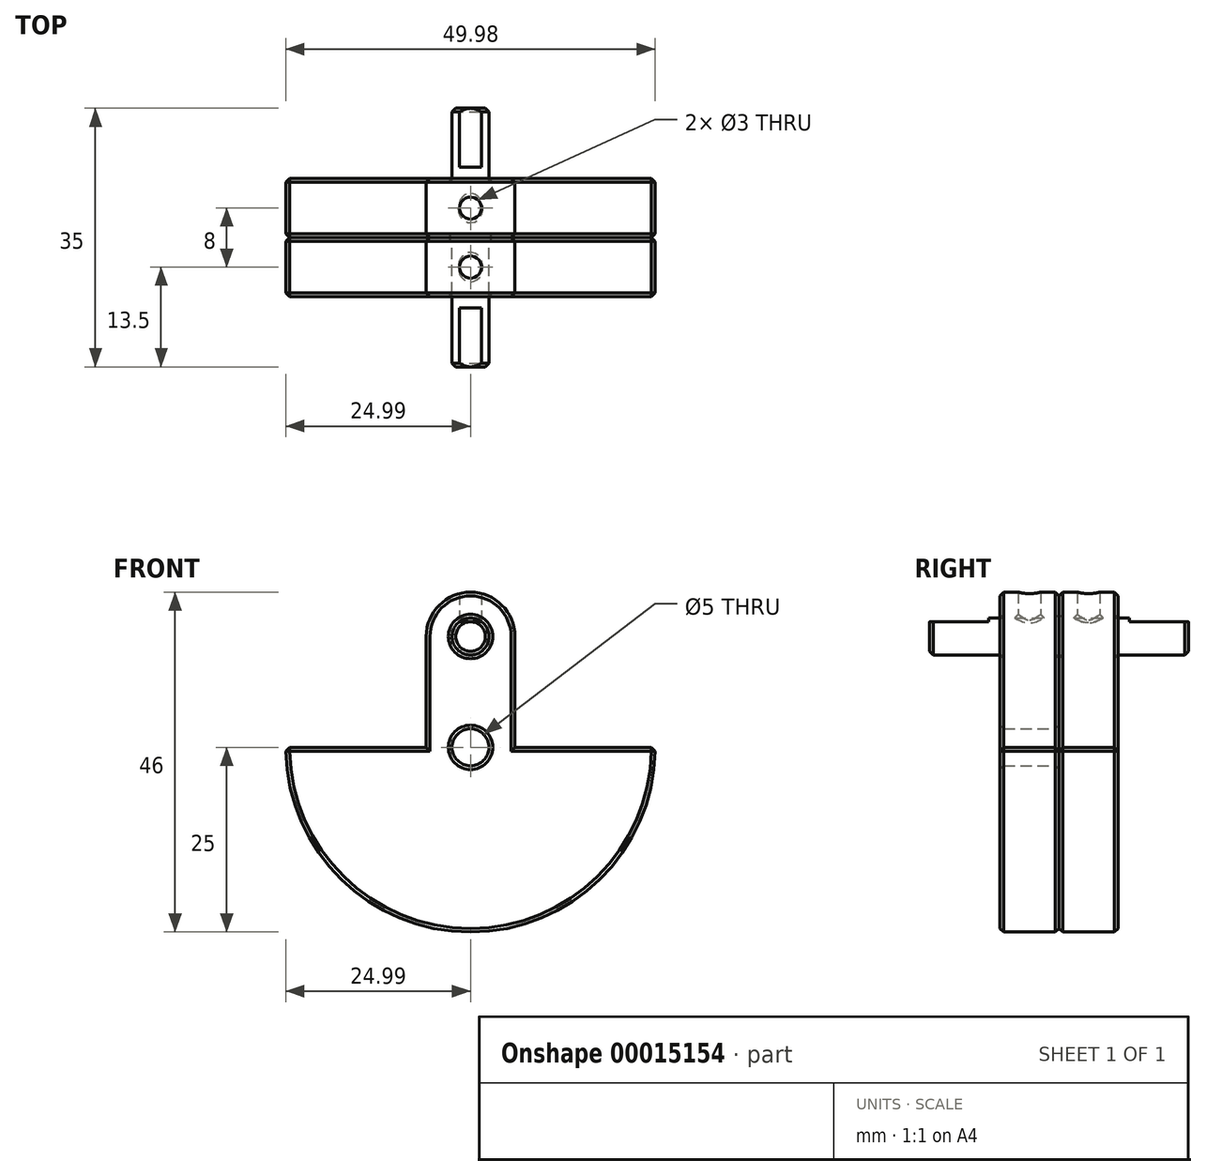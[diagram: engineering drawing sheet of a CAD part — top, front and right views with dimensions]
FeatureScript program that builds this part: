
annotation { "Feature Type Name" : "Feature", "Feature Type Description" : "" }
export const myFeature = defineFeature(function(context is Context, id is Id, definition is map)
    precondition{}
    {
        {
            var Q0;
            Q0=qCreatedBy(makeId("Front.planeOp"),FACE);
            var sketch = newSketch(context, id + "F0", { "sketchPlane" : qUnion([Q0])});
            skCircle(sketch, "E0", {"center": v(0, 0) * mm, "radius": 2.5 * mm});
            skCircle(sketch, "E1", {"center": v(0, 15) * mm, "radius": 2.5 * mm});
            skArc(sketch, "E2", {"start": v(6, 15) * mm, "mid": v(0, 21) * mm, "end": v(-6, 15) * mm});
            skLineSegment(sketch, "E3", {"start": v(-25, 0) * mm, "end": v(-6, 0) * mm});
            skLineSegment(sketch, "E4", {"start": v(-6, 15) * mm, "end": v(-6, 0) * mm});
            skLineSegment(sketch, "E5", {"start": v(6, 15) * mm, "end": v(6, 0) * mm});
            skArc(sketch, "E6", {"start": v(-25, 0) * mm, "mid": v(0, -25) * mm, "end": v(25, 0) * mm});
            skArc(sketch, "E7", {"start": v(25, 0) * mm, "mid": v(0, 25) * mm, "end": v(-25, 0) * mm, "construction": true});
            skLineSegment(sketch, "E8.trimOffspring", {"start": v(6, 0) * mm, "end": v(25, 0) * mm});
            skSolve(sketch);
        }
        {
            var Q0;
            Q0=makeQuery(id+"F0.imprint","IMPRINT",FACE,{"disambiguationData":[TD([[makeQuery(id+"F0.imprint","IMPRINT",EDGE,{"derivedFrom":sQuery(id+"F0.wireOp",EDGE,"E0")}),-1.0]])]});
            extrude(context, id + "F1", {"entities" : qUnion([Q0]), "depth" : 8 * mm});
        }
        {
            var Q0;
            Q0=makeQuery(id+"F0.imprint","IMPRINT",FACE,{"disambiguationData":[TD([[makeQuery(id+"F0.imprint","IMPRINT",EDGE,{"derivedFrom":sQuery(id+"F0.wireOp",EDGE,"E0")}),-1.0]])]});
            var Q1;
            Q1=makeQuery(id+"F0.imprint","IMPRINT",FACE,{"disambiguationData":[TD([[makeQuery(id+"F0.imprint","IMPRINT",EDGE,{"derivedFrom":sQuery(id+"F0.wireOp",EDGE,"E0")}),1.0]])]});
            extrude(context, id + "F2", {"entities" : qUnion([Q0, Q1]), "oppositeDirection" : true, "depth" : 8 * mm});
        }
        {
            var Q0;
            Q0=qCreatedBy(makeId("Top.planeOp"),FACE);
            cPlane(context, id + "F3", {"entities" : qUnion([Q0]), "cplaneType" : CPlaneType.OFFSET, "offset" : 15 * mm, "width" : 150 * mm, "height" : 150 * mm});
        }
        {
            var Q0;
            Q0=qCreatedBy(id+"F3.planeOp",FACE);
            var sketch = newSketch(context, id + "F4", { "sketchPlane" : qUnion([Q0])});
            skLineSegment(sketch, "E9", {"start": v(0, 14.38) * mm, "end": v(0, -14.54) * mm, "construction": true});
            skCircle(sketch, "E10", {"center": v(0, 4) * mm, "radius": 1.5 * mm});
            skCircle(sketch, "E11", {"center": v(0, -4) * mm, "radius": 1.5 * mm});
            skSolve(sketch);
        }
        {
            var Q0;
            Q0=makeQuery(id+"F4.imprint","IMPRINT",FACE,{"disambiguationData":[TD([[makeQuery(id+"F4.imprint","IMPRINT",EDGE,{"derivedFrom":sQuery(id+"F4.wireOp",EDGE,"E10")}),1.0]])]});
            var Q1;
            Q1=makeQuery(id+"F4.imprint","IMPRINT",FACE,{"disambiguationData":[TD([[makeQuery(id+"F4.imprint","IMPRINT",EDGE,{"derivedFrom":sQuery(id+"F4.wireOp",EDGE,"E11")}),1.0]])]});
            var Q2;
            Q2=sQuery(id+"F4.wireOp",EDGE,"E11");
            var Q3;
            Q3=sQuery(id+"F4.wireOp",EDGE,"E10");
            extrude(context, id + "F5", {"entities" : qUnion([Q0, Q1]), "operationType" : NewBodyOperationType.REMOVE, "surfaceEntities" : qUnion([Q2, Q3]), "endBound" : BoundingType.THROUGH_ALL, "depth" : 25 * mm});
        }
        {
            var Q0;
            Q0=makeQuery(id+"F1.opExtrude","CAP_EDGE",EDGE,{"disambiguationData":[OSD([sQuery(id+"F0.wireOp",EDGE,"E6")])],"isStart":false});
            var Q1;
            Q1=makeQuery(id+"F1.opExtrude","SWEPT_FACE",FACE,{"disambiguationData":[OSD([sQuery(id+"F0.wireOp",EDGE,"E0")])]});
            var Q2;
            Q2=makeQuery(id+"F1.opExtrude","SWEPT_FACE",FACE,{"disambiguationData":[OSD([sQuery(id+"F0.wireOp",EDGE,"E1")])]});
            var Q3;
            Q3=makeQuery(id+"F2.opExtrude","SWEPT_FACE",FACE,{"disambiguationData":[OSD([sQuery(id+"F0.wireOp",EDGE,"E1")])]});
            var Q4;
            Q4=makeQuery(id+"F2.opExtrude","CAP_EDGE",EDGE,{"disambiguationData":[OSD([sQuery(id+"F0.wireOp",EDGE,"E6")])],"isStart":false});
            var Q5;
            Q5=makeQuery(id+"F2.opExtrude","CAP_EDGE",EDGE,{"disambiguationData":[OSD([sQuery(id+"F0.wireOp",EDGE,"E4")])],"isStart":false});
            var Q6;
            Q6=makeQuery(id+"F2.opExtrude","CAP_EDGE",EDGE,{"disambiguationData":[OSD([sQuery(id+"F0.wireOp",EDGE,"E5")])],"isStart":false});
            var Q7;
            Q7=makeQuery(id+"F1.opExtrude","CAP_EDGE",EDGE,{"disambiguationData":[OSD([sQuery(id+"F0.wireOp",EDGE,"E5")])],"isStart":false});
            var Q8;
            Q8=makeQuery(id+"F1.opExtrude","CAP_FACE",FACE,{"disambiguationData":[OSD([sQuery(id+"F0.wireOp",EDGE,"E0"),sQuery(id+"F0.wireOp",EDGE,"E1"),sQuery(id+"F0.wireOp",EDGE,"E2"),sQuery(id+"F0.wireOp",EDGE,"E3"),sQuery(id+"F0.wireOp",EDGE,"E4"),sQuery(id+"F0.wireOp",EDGE,"E5"),sQuery(id+"F0.wireOp",EDGE,"E6"),sQuery(id+"F0.wireOp",EDGE,"E8.trimOffspring")])],"isStart":false});
            var Q9;
            Q9=makeQuery(id+"F2.opExtrude","CAP_FACE",FACE,{"disambiguationData":[OSD([sQuery(id+"F0.wireOp",EDGE,"E1"),sQuery(id+"F0.wireOp",EDGE,"E2"),sQuery(id+"F0.wireOp",EDGE,"E3"),sQuery(id+"F0.wireOp",EDGE,"E4"),sQuery(id+"F0.wireOp",EDGE,"E5"),sQuery(id+"F0.wireOp",EDGE,"E6"),sQuery(id+"F0.wireOp",EDGE,"E8.trimOffspring")])],"isStart":false});
            var Q10;
            Q10=makeQuery(id+"F2.opExtrude","CAP_FACE",FACE,{"disambiguationData":[OSD([sQuery(id+"F0.wireOp",EDGE,"E1"),sQuery(id+"F0.wireOp",EDGE,"E2"),sQuery(id+"F0.wireOp",EDGE,"E3"),sQuery(id+"F0.wireOp",EDGE,"E4"),sQuery(id+"F0.wireOp",EDGE,"E5"),sQuery(id+"F0.wireOp",EDGE,"E6"),sQuery(id+"F0.wireOp",EDGE,"E8.trimOffspring")])],"isStart":true});
            var Q11;
            Q11=makeQuery(id+"F1.opExtrude","CAP_FACE",FACE,{"disambiguationData":[OSD([sQuery(id+"F0.wireOp",EDGE,"E0"),sQuery(id+"F0.wireOp",EDGE,"E1"),sQuery(id+"F0.wireOp",EDGE,"E2"),sQuery(id+"F0.wireOp",EDGE,"E3"),sQuery(id+"F0.wireOp",EDGE,"E4"),sQuery(id+"F0.wireOp",EDGE,"E5"),sQuery(id+"F0.wireOp",EDGE,"E6"),sQuery(id+"F0.wireOp",EDGE,"E8.trimOffspring")])],"isStart":true});
            var Q12;
            Q12=makeQuery(id+"F1.opExtrude","SWEPT_EDGE",EDGE,{"disambiguationData":[OSD([sQuery(id+"F0.wireOp",EDGE,"E3"),sQuery(id+"F0.wireOp",EDGE,"E6")])]});
            var Q13;
            Q13=makeQuery(id+"F2.opExtrude","SWEPT_EDGE",EDGE,{"disambiguationData":[OSD([sQuery(id+"F0.wireOp",EDGE,"E3"),sQuery(id+"F0.wireOp",EDGE,"E6")])]});
            var Q14;
            Q14=makeQuery(id+"F1.opExtrude","SWEPT_EDGE",EDGE,{"disambiguationData":[OSD([sQuery(id+"F0.wireOp",EDGE,"E6"),sQuery(id+"F0.wireOp",EDGE,"E8.trimOffspring")])]});
            var Q15;
            Q15=makeQuery(id+"F2.opExtrude","SWEPT_EDGE",EDGE,{"disambiguationData":[OSD([sQuery(id+"F0.wireOp",EDGE,"E6"),sQuery(id+"F0.wireOp",EDGE,"E8.trimOffspring")])]});
            chamfer(context, id + "F6", {"entities" : qUnion([Q0, Q1, Q2, Q3, Q4, Q5, Q6, Q7, Q8, Q9, Q10, Q11, Q12, Q13, Q14, Q15]), "width" : .5 * mm, "tangentPropagation" : true});
        }
        {
            var Q0;
            Q0=makeQuery(id+"F0.imprint","IMPRINT",FACE,{"disambiguationData":[TD([[makeQuery(id+"F0.imprint","IMPRINT",EDGE,{"derivedFrom":sQuery(id+"F0.wireOp",EDGE,"E1")}),1.0]])]});
            extrude(context, id + "F7", {"entities" : qUnion([Q0]), "depth" : (35 / 2) * mm});
        }
        {
            var Q0;
            Q0=makeQuery(id+"F7.opExtrude","CAP_FACE",FACE,{"disambiguationData":[OSD([sQuery(id+"F0.wireOp",EDGE,"E1")])],"isStart":false});
            var sketch = newSketch(context, id + "F8", { "sketchPlane" : qUnion([Q0])});
            skLineSegment(sketch, "E12.bottom", {"start": v(-4.96, 19.77) * mm, "end": v(5.5, 19.77) * mm});
            skLineSegment(sketch, "E12.top", {"start": v(-4.96, 17) * mm, "end": v(5.5, 17) * mm});
            skLineSegment(sketch, "E12.left", {"start": v(-4.96, 19.77) * mm, "end": v(-4.96, 17) * mm});
            skLineSegment(sketch, "E12.right", {"start": v(5.5, 19.77) * mm, "end": v(5.5, 17) * mm});
            skPoint(sketch, "E13.0", {"position": v(0, 15) * mm});
            skSolve(sketch);
        }
        {
            var Q0;
            Q0=makeQuery(id+"F8.imprint","IMPRINT",FACE,{"disambiguationData":[TD([[makeQuery(id+"F8.imprint","IMPRINT",EDGE,{"derivedFrom":sQuery(id+"F8.wireOp",EDGE,"E12.bottom")}),-1.0]])]});
            var Q1;
            {var subQ0=makeQuery(id+"F7.opExtrude","CAP_EDGE",EDGE,{"disambiguationData":[OSD([sQuery(id+"F0.wireOp",EDGE,"E1")])],"isStart":false});var subQ1=sQuery(id+"F8.wireOp",EDGE,"E12.top");var subQ3=makeQuery(id+"F8.imprint","INTERSECT",VERTEX,{"disambiguationData":[OD(0.0)],"derivedFrom":[subQ0,subQ1]});Q1=makeQuery(id+"F8.imprint","IMPRINT",FACE,{"disambiguationData":[TD([[makeQuery(id+"F8.imprint","IMPRINT",EDGE,{"disambiguationData":[TD([[subQ3,-1.0]])],"derivedFrom":subQ1}),1.0]])]});}
            extrude(context, id + "F9", {"entities" : qUnion([Q0, Q1]), "operationType" : NewBodyOperationType.REMOVE, "oppositeDirection" : true, "depth" : 8 * mm});
        }
        {
            var Q0;
            Q0=makeQuery(id+"F7.opExtrude","CAP_EDGE",EDGE,{"disambiguationData":[OSD([sQuery(id+"F0.wireOp",EDGE,"E1")])],"isStart":false});
            chamfer(context, id + "F10", {"entities" : qUnion([Q0]), "width" : .5 * mm, "tangentPropagation" : true});
        }
        {
            var Q0;
            Q0=makeQuery(id+"F7.opExtrude","SWEPT_BODY",BODY,{"disambiguationData":[OSD([sQuery(id+"F0.wireOp",EDGE,"E1")])]});
            var Q1;
            Q1=makeQuery(id+"F0.imprint","IMPRINT",FACE,{"disambiguationData":[TD([[makeQuery(id+"F0.imprint","IMPRINT",EDGE,{"derivedFrom":sQuery(id+"F0.wireOp",EDGE,"E1")}),1.0]])]});
            mirror(context, id + "F11", {"operationType" : NewBodyOperationType.ADD, "entities" : qUnion([Q0]), "mirrorPlane" : qUnion([Q1])});
        }
    });
